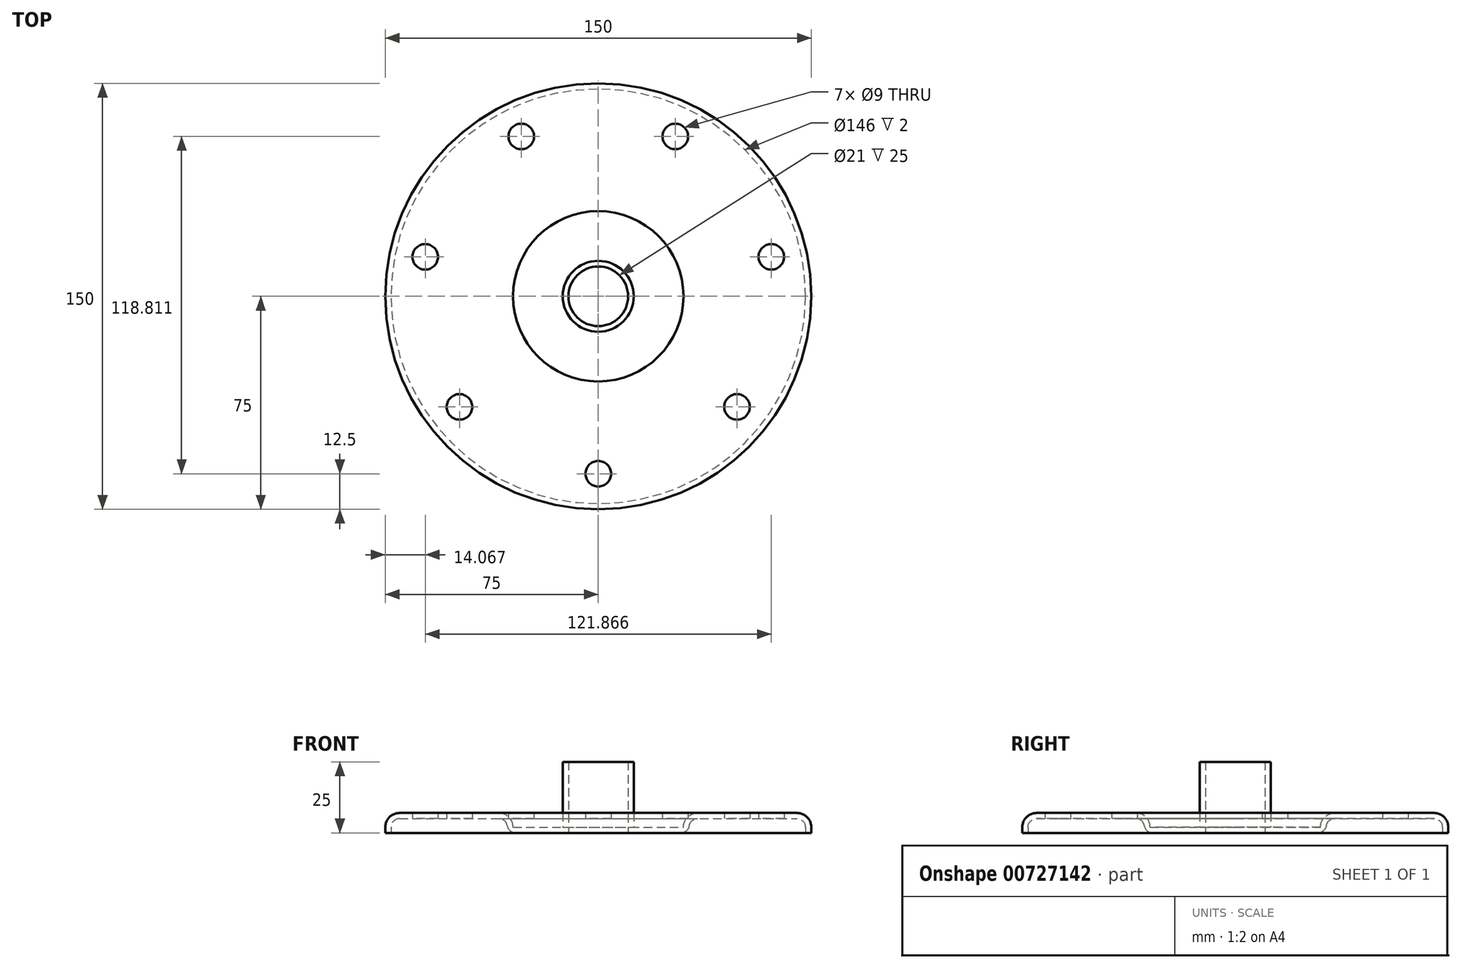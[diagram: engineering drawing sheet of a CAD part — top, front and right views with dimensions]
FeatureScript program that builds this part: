
annotation { "Feature Type Name" : "Feature", "Feature Type Description" : "" }
export const myFeature = defineFeature(function(context is Context, id is Id, definition is map)
    precondition{}
    {
        {
            var Q0;
            Q0=qCreatedBy(makeId("Front.planeOp"),FACE);
            var sketch = newSketch(context, id + "F0", { "sketchPlane" : qUnion([Q0])});
            skLineSegment(sketch, "E0", {"start": v(-35, 5) * mm, "end": v(-70, 5) * mm});
            skLineSegment(sketch, "E1", {"start": v(-30, 0) * mm, "end": v(-12.5, 0) * mm});
            skLineSegment(sketch, "E2", {"start": v(-12.5, 0) * mm, "end": v(-12.5, 23) * mm});
            skLineSegment(sketch, "E3", {"start": v(-12.5, 23) * mm, "end": v(-10.5, 23) * mm});
            skLineSegment(sketch, "E4", {"start": v(-10.5, 23) * mm, "end": v(-10.5, -2) * mm});
            skArc(sketch, "E5", {"start": v(-30, 0) * mm, "mid": v(-31.46, 3.54) * mm, "end": v(-35, 5) * mm});
            skArc(sketch, "E6", {"start": v(-70, 5) * mm, "mid": v(-73.54, 3.54) * mm, "end": v(-75, 0) * mm});
            skLineSegment(sketch, "E7", {"start": v(-70, 3) * mm, "end": v(-35, 3) * mm});
            skArc(sketch, "E8", {"start": v(-32, 0) * mm, "mid": v(-32.88, 2.12) * mm, "end": v(-35, 3) * mm});
            skArc(sketch, "E9", {"start": v(-70, 3) * mm, "mid": v(-72.12, 2.12) * mm, "end": v(-73, 0) * mm});
            skLineSegment(sketch, "E10", {"start": v(0, 0) * mm, "end": v(0, 23) * mm, "construction": true});
            skLineSegment(sketch, "E11", {"start": v(-73, 0) * mm, "end": v(-73, -2) * mm});
            skLineSegment(sketch, "E12", {"start": v(-73, -2) * mm, "end": v(-75, -2) * mm});
            skLineSegment(sketch, "E13", {"start": v(-75, -2) * mm, "end": v(-75, 0) * mm});
            skLineSegment(sketch, "E14", {"start": v(-32, 0) * mm, "end": v(-32, -2) * mm});
            skLineSegment(sketch, "E15", {"start": v(-32, -2) * mm, "end": v(-10.5, -2) * mm});
            skSolve(sketch);
        }
        {
            var Q0;
            Q0 = qSketchRegion(id + "F0", true);
            var Q1;
            Q1=sQuery(id+"F0.wireOp",EDGE,"E10");
            revolve(context, id + "F1", {"surfaceOperationType" : NewSurfaceOperationType.NEW, "entities" : qUnion([Q0]), "axis" : qUnion([Q1]), "revolveType" : RevolveType.FULL});
        }
        {
            var Q0;
            Q0=qCreatedBy(makeId("Top.planeOp"),FACE);
            var sketch = newSketch(context, id + "F2", { "sketchPlane" : qUnion([Q0])});
            skCircle(sketch, "E16", {"center": v(0, 0) * mm, "radius": 62.5 * mm, "construction": true});
            skCircle(sketch, "E17", {"center": v(0, -62.5) * mm, "radius": 4.5 * mm});
            skCircle(sketch, "E18.1.0", {"center": v(48.86, -38.97) * mm, "radius": 4.5 * mm});
            skCircle(sketch, "E18.2.0", {"center": v(60.93, 13.9) * mm, "radius": 4.5 * mm});
            skCircle(sketch, "E18.3.0", {"center": v(27.12, 56.31) * mm, "radius": 4.5 * mm});
            skCircle(sketch, "E18.4.0", {"center": v(-27.12, 56.31) * mm, "radius": 4.5 * mm});
            skCircle(sketch, "E18.5.0", {"center": v(-60.93, 13.9) * mm, "radius": 4.5 * mm});
            skCircle(sketch, "E18.6.0", {"center": v(-48.86, -38.97) * mm, "radius": 4.5 * mm});
            skSolve(sketch);
        }
        {
            var Q0;
            Q0 = qSketchRegion(id + "F2", true);
            extrude(context, id + "F3", {"entities" : qUnion([Q0]), "operationType" : NewBodyOperationType.REMOVE, "depth" : 25 * mm, "offsetDistance" : 25 * mm});
        }
        {
            var Q0;
            Q0=makeQuery(id+"F1.opRevolve","SWEPT_EDGE",EDGE,{"disambiguationData":[OSD([sQuery(id+"F0.wireOp",EDGE,"E14"),sQuery(id+"F0.wireOp",EDGE,"E15")])]});
            fillet(context, id + "F4", {"entities" : qUnion([Q0]), "radius" : 3 * mm, "tangentPropagation" : true, "allowEdgeOverflow" : false});
        }
    });
